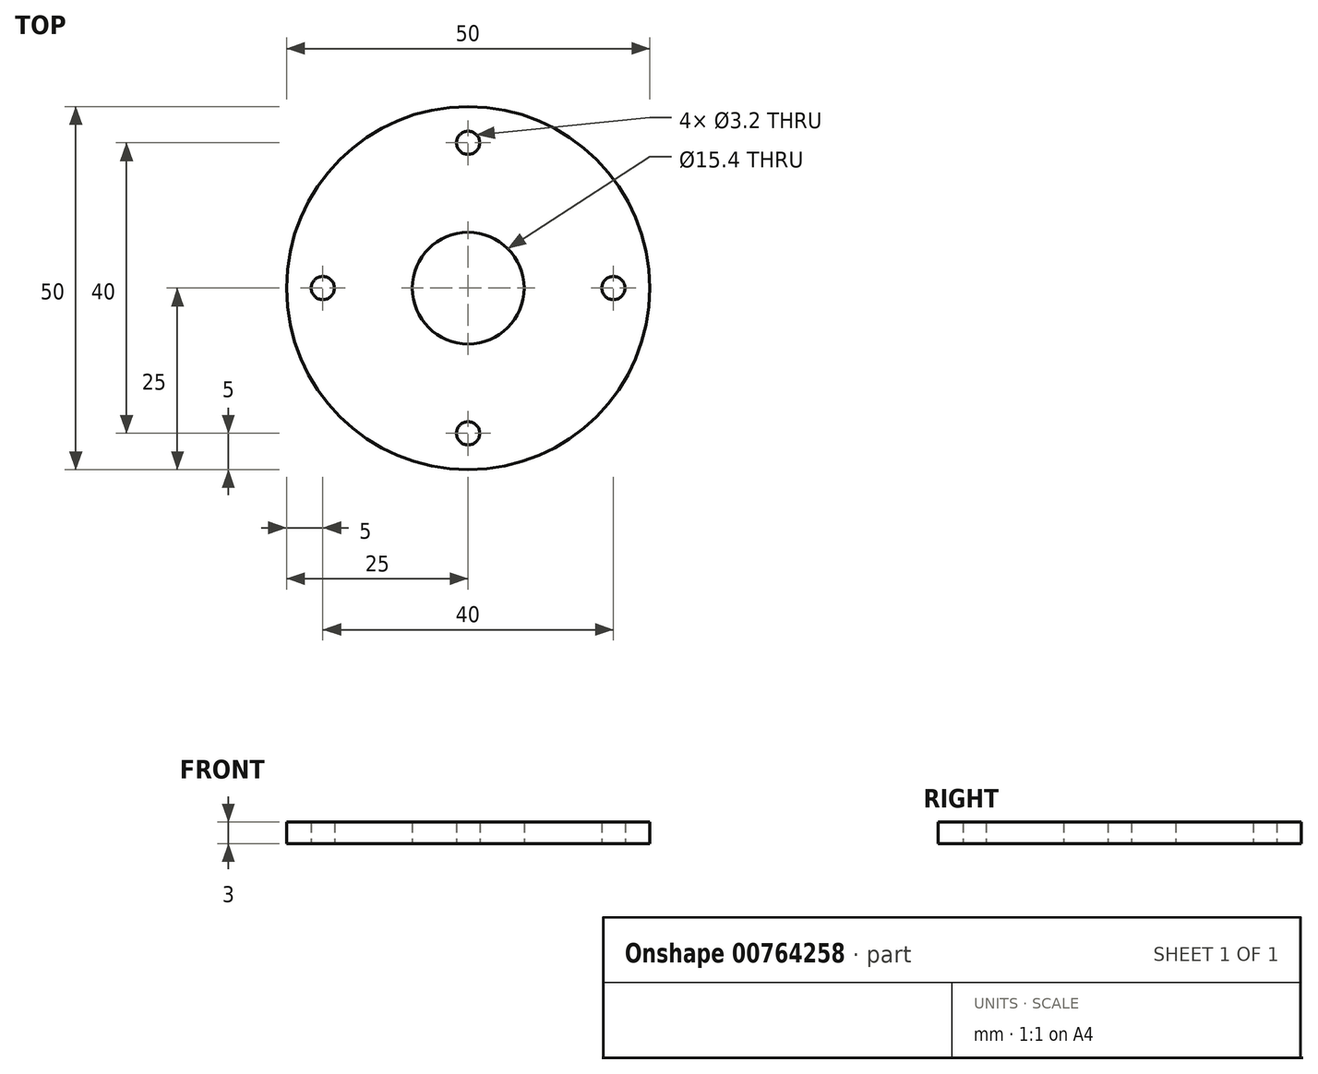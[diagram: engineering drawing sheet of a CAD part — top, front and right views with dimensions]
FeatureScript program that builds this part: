
annotation { "Feature Type Name" : "Feature", "Feature Type Description" : "" }
export const myFeature = defineFeature(function(context is Context, id is Id, definition is map)
    precondition{}
    {
        {
            var Q0;
            Q0=qCreatedBy(makeId("Top.planeOp"),FACE);
            var sketch = newSketch(context, id + "F0", { "sketchPlane" : qUnion([Q0])});
            skArc(sketch, "E0", {"start": v(24.04, -6.85) * mm, "mid": v(-17.68, 17.68) * mm, "end": v(6.85, -24.04) * mm});
            skCircle(sketch, "E1", {"center": v(0, 20) * mm, "radius": 1.6 * mm});
            skCircle(sketch, "E2", {"center": v(20, 0) * mm, "radius": 1.6 * mm});
            skCircle(sketch, "E3", {"center": v(0, -20) * mm, "radius": 1.6 * mm});
            skCircle(sketch, "E4", {"center": v(-20, 0) * mm, "radius": 1.6 * mm});
            skCircle(sketch, "E5", {"center": v(0, 0) * mm, "radius": 7.7 * mm});
            skLineSegment(sketch, "E6", {"start": v(-5.44, -5.44) * mm, "end": v(8.15, -19.04) * mm});
            skLineSegment(sketch, "E7", {"start": v(0, 0) * mm, "end": v(-5.44, -5.44) * mm});
            skLineSegment(sketch, "E8", {"start": v(5.44, 5.44) * mm, "end": v(19.04, -8.15) * mm});
            skPoint(sketch, "E9.visualSharp", {"position": v(11.37, -22.26) * mm});
            skArc(sketch, "E9.filletArc", {"start": v(6.85, -24.04) * mm, "mid": v(8.93, -21.91) * mm, "end": v(8.15, -19.04) * mm});
            skPoint(sketch, "E10.visualSharp", {"position": v(22.26, -11.37) * mm});
            skArc(sketch, "E10.filletArc", {"start": v(19.04, -8.15) * mm, "mid": v(21.91, -8.93) * mm, "end": v(24.04, -6.85) * mm});
            skCircle(sketch, "E11", {"center": v(0, 0) * mm, "radius": 25 * mm});
            skSolve(sketch);
        }
        {
            var Q0;
            Q0=makeQuery(id+"F0.imprint","IMPRINT",FACE,{"disambiguationData":[TD([[makeQuery(id+"F0.imprint","IMPRINT",EDGE,{"derivedFrom":sQuery(id+"F0.wireOp",EDGE,"E1")}),-1.0]])]});
            var Q1;
            {var subQ2=sQuery(id+"F0.wireOp",EDGE,"E6");Q1=makeQuery(id+"F0.imprint","IMPRINT",FACE,{"disambiguationData":[TD([[makeQuery(id+"F0.imprint","IMPRINT",EDGE,{"derivedFrom":subQ2}),1.0]])]});}
            extrude(context, id + "F1", {"entities" : qUnion([Q0, Q1]), "depth" : 3 * mm, "offsetDistance" : 25 * mm});
        }
    });
